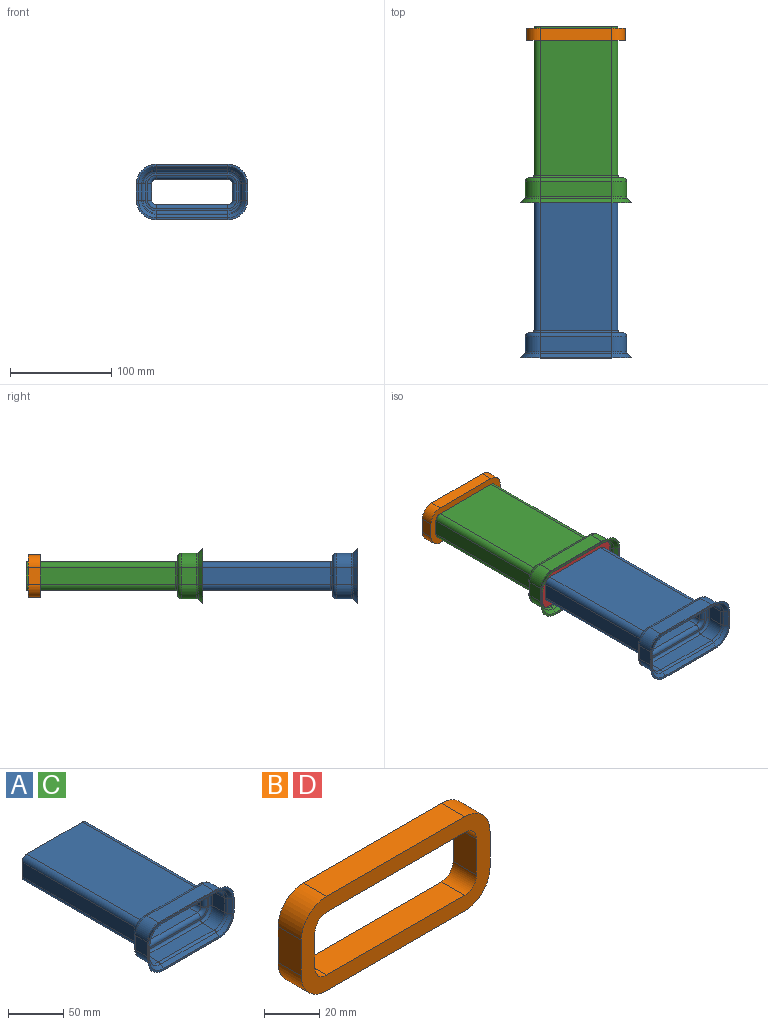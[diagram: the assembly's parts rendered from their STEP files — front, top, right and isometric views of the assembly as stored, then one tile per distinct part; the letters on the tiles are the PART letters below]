
ASSEMBLY  parts=4 mates=1
PART A: 100 faces, bbox 110x175x55 mm
  f0: plane 83x28mm, normal (0,1,0), area 310.5mm2, adj f1,f2,f3,f4,f5,f6,f7,f8
  f1: plane 147.5x16mm, normal (1,0,0), area 2360mm2, adj f0,f5,f8,f46
  f2: plane 147.5x71mm, normal (0,0,1), area 10472.5mm2, adj f0,f5,f6,f43
  f3: plane 147.5x16mm, normal (-1,0,0), area 2360mm2, adj f0,f6,f7,f47
  f4: plane 147.5x71mm, normal (0,0,-1), area 10472.5mm2, adj f0,f7,f8,f50
  f5: cylinder r=6mm len=147.5mm, axis (0,-1,0), area 1390.2mm2, adj f0,f1,f2,f44
  f6: cylinder r=6mm len=147.5mm, axis (0,1,0), area 1390.2mm2, adj f0,f2,f3,f45
  f7: cylinder r=6mm len=147.5mm, axis (0,-1,0), area 1390.2mm2, adj f0,f3,f4,f49
  f8: cylinder r=6mm len=147.5mm, axis (0,1,0), area 1390.2mm2, adj f0,f1,f4,f48
  f9: plane 92x37mm, normal (0,1,0), area 467.4mm2, adj f27,f28,f29,f30,f31,f32,f33,f34
  f10: plane 16x14.96mm, normal (1,0,0), area 239.4mm2, adj f11,f17,f30,f39
  f11: cylinder r=14.5mm len=14.96mm, axis (0,1,0), area 340.8mm2, adj f10,f12,f32,f37
  f12: plane 71x14.96mm, normal (0,0,1), area 1062.5mm2, adj f11,f13,f34,f35
  f13: cylinder r=14.5mm len=14.96mm, axis (0,1,0), area 340.8mm2, adj f12,f14,f33,f36
  f14: plane 16x14.96mm, normal (-1,0,0), area 239.4mm2, adj f13,f15,f31,f38
  f15: cylinder r=14.5mm len=14.96mm, axis (0,1,0), area 340.8mm2, adj f14,f16,f29,f40
  f16: plane 71x14.96mm, normal (0,0,-1), area 1062.5mm2, adj f15,f17,f27,f42
  f17: cylinder r=14.5mm len=14.96mm, axis (0,1,0), area 340.8mm2, adj f10,f16,f28,f41
  f18: cone r=14.5mm half-angle=45deg, axis (0,-1,0), area 164.6mm2, adj f19,f25,f26,f41
  f19: plane 16x4.27mm, normal (0.71,0.71,0), area 96.6mm2, adj f18,f20,f26,f39
  f20: cone r=14.5mm half-angle=45deg, axis (0,-1,0), area 164.6mm2, adj f19,f21,f26,f37
  f21: plane 71x4.27mm, normal (0,0.71,0.71), area 428.5mm2, adj f20,f22,f26,f35
  f22: cone r=14.5mm half-angle=45deg, axis (0,-1,0), area 164.6mm2, adj f21,f23,f26,f36
  f23: plane 16x4.27mm, normal (-0.71,0.71,0), area 96.6mm2, adj f22,f24,f26,f38
  f24: cone r=14.5mm half-angle=45deg, axis (0,-1,0), area 164.6mm2, adj f23,f25,f26,f40
  f25: plane 71x4.27mm, normal (0,0.71,-0.71), area 428.5mm2, adj f18,f24,f26,f42
  f26: plane 110x55mm, normal (0,-1,0), area 614.9mm2, adj f18,f19,f20,f21,f22,f23,f24,f25
  f27: cylinder r=4mm len=71mm, axis (1,0,0), area 446.1mm2, adj f9,f16,f28,f29
  f28: torus R=10.5mm, axis (0,-1,0), area 128.8mm2, adj f9,f17,f27,f30
  f29: torus R=10.5mm, axis (0,-1,0), area 128.8mm2, adj f9,f15,f27,f31
  f30: cylinder r=4mm len=16mm, axis (0,0,1), area 100.5mm2, adj f9,f10,f28,f32
  f31: cylinder r=4mm len=16mm, axis (0,0,-1), area 100.5mm2, adj f9,f14,f29,f33
  f32: torus R=10.5mm, axis (0,-1,0), area 128.8mm2, adj f9,f11,f30,f34
  f33: torus R=10.5mm, axis (0,-1,0), area 128.8mm2, adj f9,f13,f31,f34
  f34: cylinder r=4mm len=71mm, axis (-1,0,0), area 446.1mm2, adj f9,f12,f32,f33
  f35: cylinder r=2.5mm len=71mm, axis (-1,0,0), area 139.4mm2, adj f12,f21,f36,f37
  f36: torus R=17mm, axis (0,-1,0), area 45.5mm2, adj f13,f22,f35,f38
  f37: torus R=17mm, axis (0,-1,0), area 45.5mm2, adj f11,f20,f35,f39
  f38: cylinder r=2.5mm len=16mm, axis (0,0,-1), area 31.4mm2, adj f14,f23,f36,f40
  f39: cylinder r=2.5mm len=16mm, axis (0,0,1), area 31.4mm2, adj f10,f19,f37,f41
  f40: torus R=17mm, axis (0,-1,0), area 45.5mm2, adj f15,f24,f38,f42
  f41: torus R=17mm, axis (0,-1,0), area 45.5mm2, adj f17,f18,f39,f42
  f42: cylinder r=2.5mm len=71mm, axis (1,0,0), area 139.4mm2, adj f16,f25,f40,f41
  f43: cylinder r=2.5mm len=71mm, axis (1,0,0), area 278.8mm2, adj f2,f9,f44,f45
  f44: torus R=8.5mm, axis (0,-1,0), area 42.6mm2, adj f5,f9,f43,f46
  f45: torus R=8.5mm, axis (0,-1,0), area 42.6mm2, adj f6,f9,f43,f47
  f46: cylinder r=2.5mm len=16mm, axis (0,0,-1), area 62.8mm2, adj f1,f9,f44,f48
  f47: cylinder r=2.5mm len=16mm, axis (0,0,1), area 62.8mm2, adj f3,f9,f45,f49
  f48: torus R=8.5mm, axis (0,-1,0), area 42.6mm2, adj f8,f9,f46,f50
  f49: torus R=8.5mm, axis (0,-1,0), area 42.6mm2, adj f7,f9,f47,f50
  f50: cylinder r=2.5mm len=71mm, axis (-1,0,0), area 278.8mm2, adj f4,f9,f48,f49
  f51: plane 147.5x16mm, normal (-1,0,0), area 2360mm2, adj f0,f55,f58,f95
  f52: plane 147.5x71mm, normal (0,0,-1), area 10472.5mm2, adj f0,f55,f56,f92
  f53: plane 147.5x16mm, normal (1,0,0), area 2360mm2, adj f0,f56,f57,f96
  f54: plane 147.5x71mm, normal (0,0,1), area 10472.5mm2, adj f0,f57,f58,f99
  f55: cylinder r=4.5mm len=147.5mm, axis (0,-1,0), area 1042.6mm2, adj f0,f51,f52,f93
  f56: cylinder r=4.5mm len=147.5mm, axis (0,1,0), area 1042.6mm2, adj f0,f52,f53,f94
  f57: cylinder r=4.5mm len=147.5mm, axis (0,-1,0), area 1042.6mm2, adj f0,f53,f54,f98
  f58: cylinder r=4.5mm len=147.5mm, axis (0,1,0), area 1042.6mm2, adj f0,f51,f54,f97
  f59: plane 92x37mm, normal (0,-1,0), area 467.4mm2, adj f76,f77,f78,f79,f80,f81,f82,f83
  f60: plane 16x14.96mm, normal (-1,0,0), area 239.4mm2, adj f61,f67,f79,f88
  f61: cylinder r=13mm len=14.96mm, axis (0,1,0), area 305.6mm2, adj f60,f62,f81,f86
  f62: plane 71x14.96mm, normal (0,0,-1), area 1062.5mm2, adj f61,f63,f83,f84
  f63: cylinder r=13mm len=14.96mm, axis (0,1,0), area 305.6mm2, adj f62,f64,f82,f85
  f64: plane 16x14.96mm, normal (1,0,0), area 239.4mm2, adj f63,f65,f80,f87
  f65: cylinder r=13mm len=14.96mm, axis (0,1,0), area 305.6mm2, adj f64,f66,f78,f89
  f66: plane 71x14.96mm, normal (0,0,1), area 1062.5mm2, adj f65,f67,f76,f91
  f67: cylinder r=13mm len=14.96mm, axis (0,1,0), area 305.6mm2, adj f60,f66,f77,f90
  f68: cone r=13.44mm half-angle=45deg, axis (0,-1,0), area 112.4mm2, adj f26,f69,f75,f90
  f69: plane 16x3.21mm, normal (-0.71,-0.71,0), area 72.6mm2, adj f26,f68,f70,f88
  f70: cone r=13.44mm half-angle=45deg, axis (0,-1,0), area 112.4mm2, adj f26,f69,f71,f86
  f71: plane 71x3.21mm, normal (0,-0.71,-0.71), area 322mm2, adj f26,f70,f72,f84
  f72: cone r=13.44mm half-angle=45deg, axis (0,-1,0), area 112.4mm2, adj f26,f71,f73,f85
  f73: plane 16x3.21mm, normal (0.71,-0.71,0), area 72.6mm2, adj f26,f72,f74,f87
  f74: cone r=13.44mm half-angle=45deg, axis (0,-1,0), area 112.4mm2, adj f26,f73,f75,f89
  f75: plane 71x3.21mm, normal (0,-0.71,0.71), area 322mm2, adj f26,f68,f74,f91
  f76: cylinder r=2.5mm len=71mm, axis (1,0,0), area 278.8mm2, adj f59,f66,f77,f78
  f77: torus R=10.5mm, axis (0,-1,0), area 74.6mm2, adj f59,f67,f76,f79
  f78: torus R=10.5mm, axis (0,-1,0), area 74.6mm2, adj f59,f65,f76,f80
  f79: cylinder r=2.5mm len=16mm, axis (0,0,1), area 62.8mm2, adj f59,f60,f77,f81
  f80: cylinder r=2.5mm len=16mm, axis (0,0,-1), area 62.8mm2, adj f59,f64,f78,f82
  f81: torus R=10.5mm, axis (0,-1,0), area 74.6mm2, adj f59,f61,f79,f83
  f82: torus R=10.5mm, axis (0,-1,0), area 74.6mm2, adj f59,f63,f80,f83
  f83: cylinder r=2.5mm len=71mm, axis (-1,0,0), area 278.8mm2, adj f59,f62,f81,f82
  f84: cylinder r=4mm len=71mm, axis (-1,0,0), area 223.1mm2, adj f62,f71,f85,f86
  f85: torus R=17mm, axis (0,-1,0), area 66.1mm2, adj f63,f72,f84,f87
  f86: torus R=17mm, axis (0,-1,0), area 66.1mm2, adj f61,f70,f84,f88
  f87: cylinder r=4mm len=16mm, axis (0,0,-1), area 50.3mm2, adj f64,f73,f85,f89
  f88: cylinder r=4mm len=16mm, axis (0,0,1), area 50.3mm2, adj f60,f69,f86,f90
  f89: torus R=17mm, axis (0,-1,0), area 66.1mm2, adj f65,f74,f87,f91
  f90: torus R=17mm, axis (0,-1,0), area 66.1mm2, adj f67,f68,f88,f91
  f91: cylinder r=4mm len=71mm, axis (1,0,0), area 223.1mm2, adj f66,f75,f89,f90
  f92: cylinder r=4mm len=71mm, axis (1,0,0), area 446.1mm2, adj f52,f59,f93,f94
  f93: torus R=8.5mm, axis (0,-1,0), area 58.8mm2, adj f55,f59,f92,f95
  f94: torus R=8.5mm, axis (0,-1,0), area 58.8mm2, adj f56,f59,f92,f96
  f95: cylinder r=4mm len=16mm, axis (0,0,-1), area 100.5mm2, adj f51,f59,f93,f97
  f96: cylinder r=4mm len=16mm, axis (0,0,1), area 100.5mm2, adj f53,f59,f94,f98
  f97: torus R=8.5mm, axis (0,-1,0), area 58.8mm2, adj f58,f59,f95,f99
  f98: torus R=8.5mm, axis (0,-1,0), area 58.8mm2, adj f57,f59,f96,f99
  f99: cylinder r=4mm len=71mm, axis (-1,0,0), area 446.1mm2, adj f54,f59,f97,f98
PART B: 18 faces, bbox 97x12x42 mm
  f0: cylinder r=6mm len=12mm, axis (0,1,0), area 113.1mm2, adj f1,f15,f16,f17
  f1: plane 71x12mm, normal (0,0,-1), area 852mm2, adj f0,f2,f16,f17
  f2: cylinder r=6mm len=12mm, axis (0,1,0), area 113.1mm2, adj f1,f3,f16,f17
  f3: plane 16x12mm, normal (-1,0,0), area 192mm2, adj f2,f4,f16,f17
  f4: cylinder r=6mm len=12mm, axis (0,1,0), area 113.1mm2, adj f3,f5,f16,f17
  f5: plane 71x12mm, normal (0,0,1), area 852mm2, adj f4,f6,f16,f17
  f6: cylinder r=6mm len=12mm, axis (0,1,0), area 113.1mm2, adj f5,f15,f16,f17
  f7: plane 71x12mm, normal (0,0,1), area 852mm2, adj f8,f14,f16,f17
  f8: cylinder r=13mm len=13mm, axis (0,1,0), area 245mm2, adj f7,f9,f16,f17
  f9: plane 16x12mm, normal (-1,0,0), area 192mm2, adj f8,f10,f16,f17
  f10: cylinder r=13mm len=13mm, axis (0,1,0), area 245mm2, adj f9,f11,f16,f17
  f11: plane 71x12mm, normal (0,0,-1), area 852mm2, adj f10,f12,f16,f17
  f12: cylinder r=13mm len=13mm, axis (0,1,0), area 245mm2, adj f11,f13,f16,f17
  f13: plane 16x12mm, normal (1,0,0), area 192mm2, adj f12,f14,f16,f17
  f14: cylinder r=13mm len=13mm, axis (0,1,0), area 245mm2, adj f7,f13,f16,f17
  f15: plane 16x12mm, normal (1,0,0), area 192mm2, adj f0,f6,f16,f17
  f16: plane 97x42mm, normal (0,-1,0), area 1635.8mm2, adj f0,f1,f2,f3,f4,f5,f6,f7
  f17: plane 97x42mm, normal (0,1,0), area 1635.8mm2, adj f0,f1,f2,f3,f4,f5,f6,f7
PART C: same geometry as A
PART D: same geometry as B
PLACE A t=(69.76,1.99,38.54)mm
PLACE B t=(69.76,155.47,38.54)mm
PLACE C t=(69.76,155.47,38.54)mm
PLACE D t=(69.76,1.99,38.54)mm
MATE fastened D.f11 <-> C.f66  axis (0,0,-1) through (69.76,-6.01,17.54)mm
